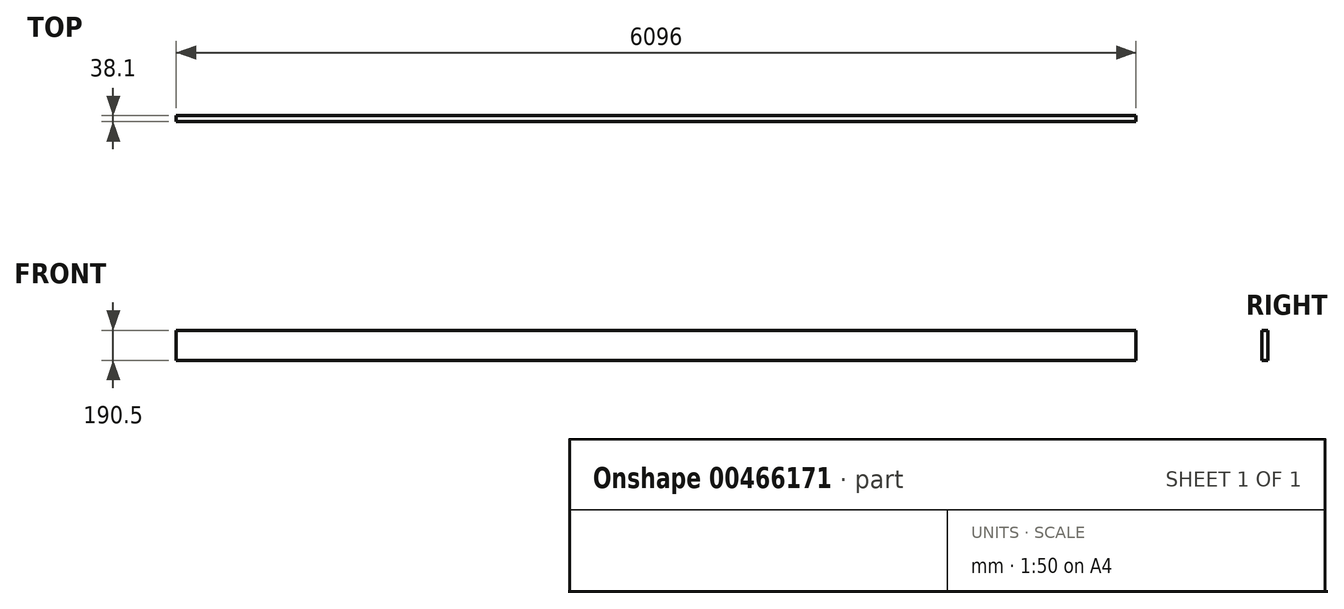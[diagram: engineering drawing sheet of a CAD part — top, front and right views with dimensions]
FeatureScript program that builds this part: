
annotation { "Feature Type Name" : "Feature", "Feature Type Description" : "" }
export const myFeature = defineFeature(function(context is Context, id is Id, definition is map)
    precondition{}
    {
        {
            var Q0;
            Q0=qCreatedBy(makeId("Right.planeOp"),FACE);
            var sketch = newSketch(context, id + "F0", { "sketchPlane" : qUnion([Q0])});
            skLineSegment(sketch, "E0.bottom", {"start": v(0, 0) * mm, "end": v(38.1, 0) * mm});
            skLineSegment(sketch, "E0.top", {"start": v(0, 190.5) * mm, "end": v(38.1, 190.5) * mm});
            skLineSegment(sketch, "E0.left", {"start": v(0, 0) * mm, "end": v(0, 190.5) * mm});
            skLineSegment(sketch, "E0.right", {"start": v(38.1, 0) * mm, "end": v(38.1, 190.5) * mm});
            skSolve(sketch);
        }
        {
            var Q0;
            Q0 = qSketchRegion(id + "F0", true);
            extrude(context, id + "F1", {"entities" : qUnion([Q0]), "oppositeDirection" : true, "depth" : 6096 * mm});
        }
    });
